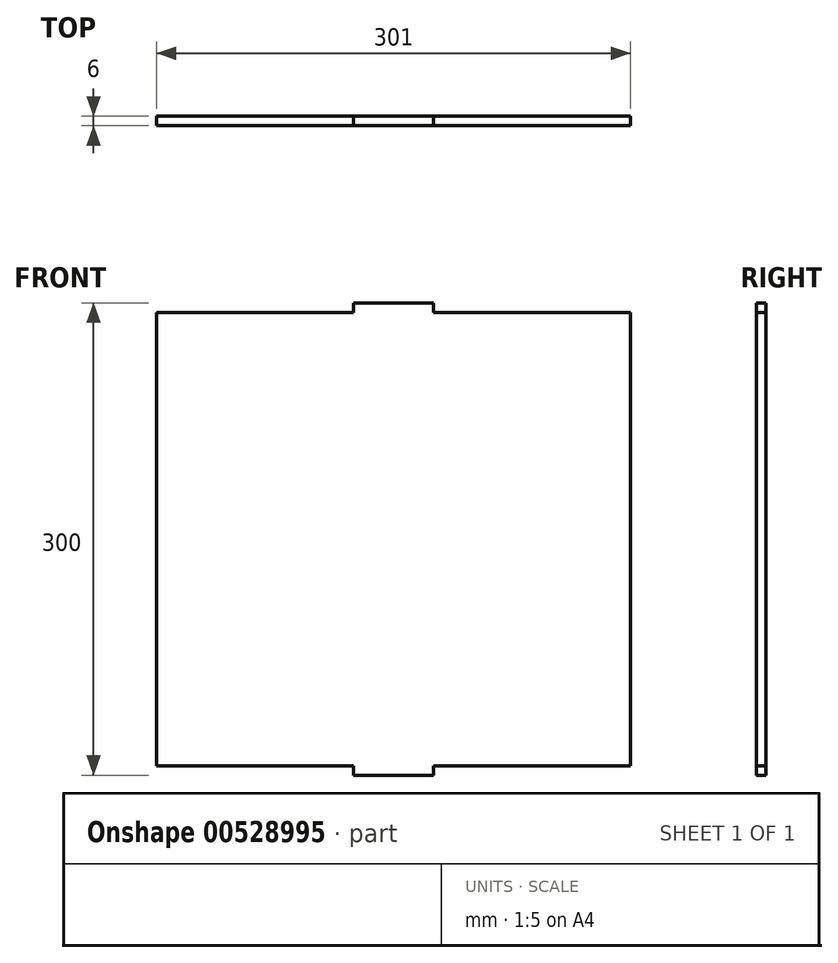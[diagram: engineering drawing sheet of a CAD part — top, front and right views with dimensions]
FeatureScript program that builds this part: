
annotation { "Feature Type Name" : "Feature", "Feature Type Description" : "" }
export const myFeature = defineFeature(function(context is Context, id is Id, definition is map)
    precondition{}
    {
        {
            var Q0;
            Q0=qCreatedBy(makeId("Front.planeOp"),FACE);
            var sketch = newSketch(context, id + "F0", { "sketchPlane" : qUnion([Q0])});
            skLineSegment(sketch, "E0.left", {"start": v(-180.97, 208.5) * mm, "end": v(-180.97, -79.5) * mm});
            skLineSegment(sketch, "E1", {"start": v(-180.97, -79.5) * mm, "end": v(-55.97, -79.5) * mm});
            skLineSegment(sketch, "E2", {"start": v(120.03, -79.5) * mm, "end": v(120.03, 208.5) * mm});
            skLineSegment(sketch, "E3", {"start": v(-55.97, 214.5) * mm, "end": v(-55.97, 208.5) * mm});
            skLineSegment(sketch, "E4", {"start": v(-4.97, 208.5) * mm, "end": v(-4.97, 214.5) * mm});
            skLineSegment(sketch, "E5", {"start": v(-55.97, 214.5) * mm, "end": v(-4.97, 214.5) * mm});
            skLineSegment(sketch, "E6", {"start": v(-55.97, 208.5) * mm, "end": v(-180.97, 208.5) * mm});
            skLineSegment(sketch, "E7", {"start": v(-4.97, 208.5) * mm, "end": v(120.03, 208.5) * mm});
            skLineSegment(sketch, "E8", {"start": v(-55.97, -79.5) * mm, "end": v(-55.97, -85.5) * mm});
            skLineSegment(sketch, "E9", {"start": v(-55.97, -85.5) * mm, "end": v(-4.97, -85.5) * mm});
            skLineSegment(sketch, "E10", {"start": v(-4.97, -85.5) * mm, "end": v(-4.97, -79.5) * mm});
            skLineSegment(sketch, "E11.trimOffspring", {"start": v(-4.97, -79.5) * mm, "end": v(120.03, -79.5) * mm});
            skSolve(sketch);
        }
        {
            var Q0;
            Q0=qSketchRegion(id+"F0",true);
            extrude(context, id + "F1", {"entities" : qUnion([Q0]), "depth" : 6 * mm});
        }
    });
